# Revit family: QF_FESTIVE_YCO9
name_source: partatom
category: Specialty Equipment
units: mm (PartAtom-declared; Revit-internal decimal feet)

## family parameters
Always vertical = Yes
Cut with Voids When Loaded = No
Part Type = Normal
Room Calculation Point = No
Round Connector Dimension = Use Diameter
Shared = No
Work Plane-Based = No

## types (3) — shared parameters
Conn Conduit = Yes
Conn Plug = 10A Plug
Cycle = 50 Hz
Depth = 640 mm  [stored 2.09974 ft]
Description = YORK CHILLED IMPULSE
Foodservice Equipment Identifier = Yes
Height = 1400 mm  [stored 4.59318 ft]
Identify Quantity as Lot = Yes
Manufacturer = FESTIVE
Max Overcurrent Protection = 0 A
Min Ckt Ampacity = 0 A
Number of Poles = 1
Phase = 1
Volts = 220 V
zero-valued in all types: Default Elevation, Elec Conn Connection Height, Elec Conn RI Height, Weight in Pounds

## per-type parameters (varying)
| type | Apparent Power | FL Amps | Length | Model | Watts |
| YCO15_220-240/50/1 | 2860 VA | 13 A | 1530 mm | YCO15 | 2860 W |
| YCO12_220-240/50/1 | 2024 VA | 9 A | 1200 mm | YCO12 | 2024 W |
| YCO9_220-240/50/1 | 1980 VA | 9 A | 900 mm  [stored 2.95276 ft] | YCO9 | 1980 W |

note: [stored X ft] marks values corroborated as IEEE doubles in the binary element streams (Revit-internal decimal feet)

## geometry (parser evidence)
native form markers: Sweep x10
no freeform markers — native parametric forms only
